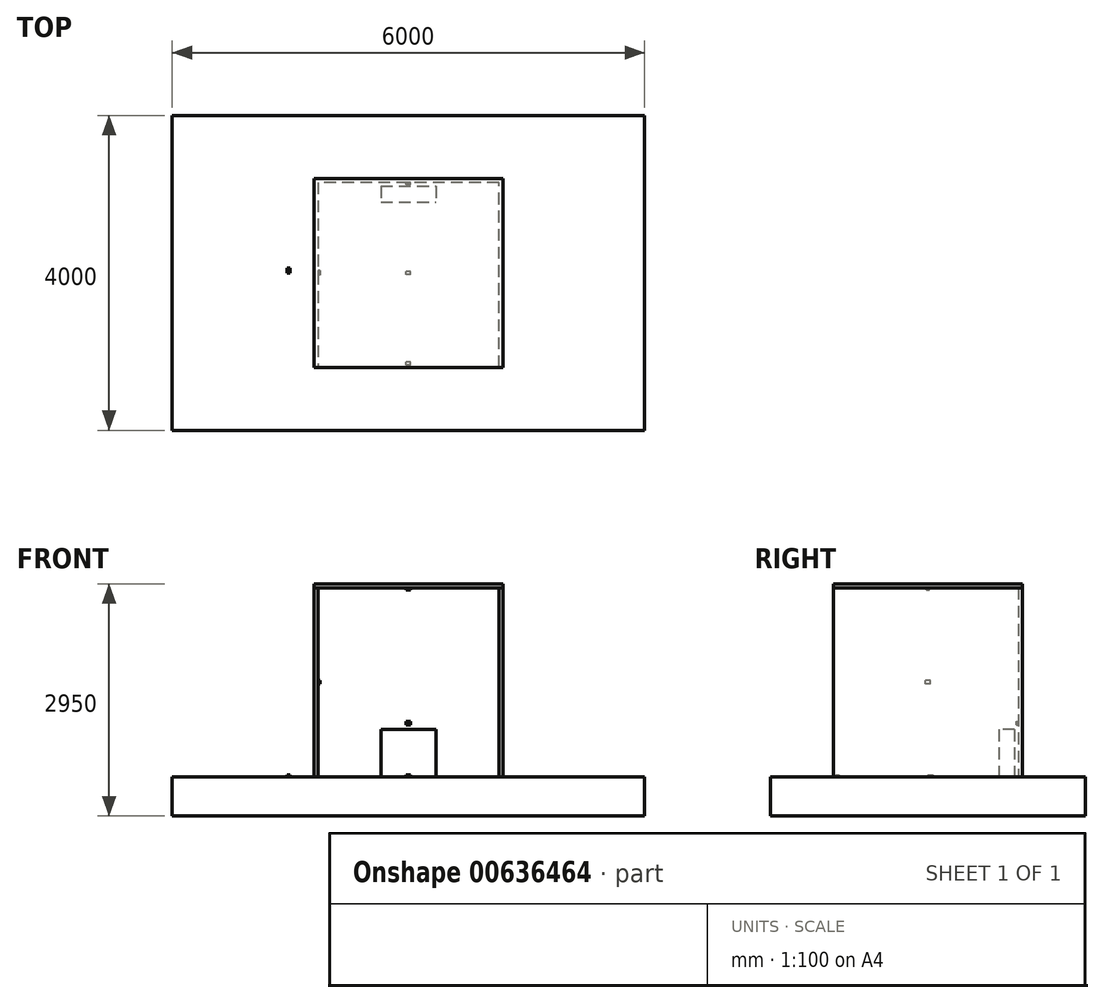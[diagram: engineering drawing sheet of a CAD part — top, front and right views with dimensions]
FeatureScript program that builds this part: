
annotation { "Feature Type Name" : "Feature", "Feature Type Description" : "" }
export const myFeature = defineFeature(function(context is Context, id is Id, definition is map)
    precondition{}
    {
        {
            var Q0;
            Q0=qCreatedBy(makeId("Top.planeOp"),FACE);
            var sketch = newSketch(context, id + "F0", { "sketchPlane" : qUnion([Q0])});
            skLineSegment(sketch, "E0.bottom", {"start": v(1200, -1200) * mm, "end": v(1150, -1200) * mm});
            skLineSegment(sketch, "E0.top", {"start": v(1200, 1200) * mm, "end": v(-1200, 1200) * mm});
            skLineSegment(sketch, "E0.left", {"start": v(1200, -1200) * mm, "end": v(1200, 1200) * mm});
            skLineSegment(sketch, "E0.right", {"start": v(-1200, -1200) * mm, "end": v(-1200, 1200) * mm});
            skPoint(sketch, "E0.middle", {"position": v(0, 0) * mm});
            skLineSegment(sketch, "E1.top", {"start": v(1150, 1150) * mm, "end": v(-1150, 1150) * mm});
            skLineSegment(sketch, "E1.left", {"start": v(1150, -1150) * mm, "end": v(1150, 1150) * mm});
            skLineSegment(sketch, "E1.right", {"start": v(-1150, -1150) * mm, "end": v(-1150, 1150) * mm});
            skLineSegment(sketch, "E2", {"start": v(-1150, -1150) * mm, "end": v(-1150, -1200) * mm});
            skLineSegment(sketch, "E3", {"start": v(1150, -1150) * mm, "end": v(1150, -1200) * mm});
            skLineSegment(sketch, "E4.trimOffspring", {"start": v(-1150, -1200) * mm, "end": v(-1200, -1200) * mm});
            skSolve(sketch);
        }
        {
            var Q0;
            Q0 = qSketchRegion(id + "F0", true);
            extrude(context, id + "F1", {"entities" : qUnion([Q0]), "endBound" : BoundingType.SYMMETRIC, "depth" : 2400 * mm, "offsetDistance" : 25 * mm});
        }
        {
            var Q0;
            Q0=makeQuery(id+"F1.opExtrude","CAP_FACE",FACE,{"disambiguationData":[OSD([sQuery(id+"F0.wireOp",EDGE,"E0.bottom"),sQuery(id+"F0.wireOp",EDGE,"E0.top"),sQuery(id+"F0.wireOp",EDGE,"E0.left"),sQuery(id+"F0.wireOp",EDGE,"E0.right"),sQuery(id+"F0.wireOp",EDGE,"E1.top"),sQuery(id+"F0.wireOp",EDGE,"E1.left"),sQuery(id+"F0.wireOp",EDGE,"E1.right"),sQuery(id+"F0.wireOp",EDGE,"E2"),sQuery(id+"F0.wireOp",EDGE,"E3"),sQuery(id+"F0.wireOp",EDGE,"E4.trimOffspring")])],"isStart":false});
            var sketch = newSketch(context, id + "F2", { "sketchPlane" : qUnion([Q0])});
            skLineSegment(sketch, "E5.bottom", {"start": v(1200, -1200) * mm, "end": v(-1200, -1200) * mm});
            skLineSegment(sketch, "E5.top", {"start": v(1200, 1200) * mm, "end": v(-1200, 1200) * mm});
            skLineSegment(sketch, "E5.left", {"start": v(1200, -1200) * mm, "end": v(1200, 1200) * mm});
            skLineSegment(sketch, "E5.right", {"start": v(-1200, -1200) * mm, "end": v(-1200, 1200) * mm});
            skSolve(sketch);
        }
        {
            var Q0;
            Q0 = qSketchRegion(id + "F2", true);
            extrude(context, id + "F3", {"entities" : qUnion([Q0]), "depth" : 50 * mm, "offsetDistance" : 25 * mm});
        }
        {
            var Q0;
            Q0=makeQuery(id+"F1.opExtrude","CAP_FACE",FACE,{"disambiguationData":[OSD([sQuery(id+"F0.wireOp",EDGE,"E0.bottom"),sQuery(id+"F0.wireOp",EDGE,"E0.top"),sQuery(id+"F0.wireOp",EDGE,"E0.left"),sQuery(id+"F0.wireOp",EDGE,"E0.right"),sQuery(id+"F0.wireOp",EDGE,"E1.top"),sQuery(id+"F0.wireOp",EDGE,"E1.left"),sQuery(id+"F0.wireOp",EDGE,"E1.right"),sQuery(id+"F0.wireOp",EDGE,"E2"),sQuery(id+"F0.wireOp",EDGE,"E3"),sQuery(id+"F0.wireOp",EDGE,"E4.trimOffspring")])],"isStart":true});
            var sketch = newSketch(context, id + "F4", { "sketchPlane" : qUnion([Q0])});
            skLineSegment(sketch, "E6.bottom", {"start": v(3000, -2000) * mm, "end": v(-3000, -2000) * mm});
            skLineSegment(sketch, "E6.top", {"start": v(3000, 2000) * mm, "end": v(-3000, 2000) * mm});
            skLineSegment(sketch, "E6.left", {"start": v(3000, -2000) * mm, "end": v(3000, 2000) * mm});
            skLineSegment(sketch, "E6.right", {"start": v(-3000, -2000) * mm, "end": v(-3000, 2000) * mm});
            skPoint(sketch, "E6.middle", {"position": v(0, 0) * mm});
            skSolve(sketch);
        }
        {
            var Q0;
            Q0 = qSketchRegion(id + "F4", true);
            extrude(context, id + "F5", {"entities" : qUnion([Q0]), "operationType" : NewBodyOperationType.ADD, "depth" : 500 * mm, "offsetDistance" : 25 * mm});
        }
        {
            var Q0;
            Q0=makeQuery(id+"F5.opExtrude","CAP_FACE",FACE,{"disambiguationData":[OSD([sQuery(id+"F4.wireOp",EDGE,"E6.bottom"),sQuery(id+"F4.wireOp",EDGE,"E6.top"),sQuery(id+"F4.wireOp",EDGE,"E6.left"),sQuery(id+"F4.wireOp",EDGE,"E6.right")])],"isStart":true});
            var sketch = newSketch(context, id + "F6", { "sketchPlane" : qUnion([Q0])});
            skLineSegment(sketch, "E7.bottom", {"start": v(-350, 1100) * mm, "end": v(350, 1100) * mm});
            skLineSegment(sketch, "E7.top", {"start": v(-350, 900) * mm, "end": v(350, 900) * mm});
            skLineSegment(sketch, "E7.left", {"start": v(-350, 1100) * mm, "end": v(-350, 900) * mm});
            skLineSegment(sketch, "E7.right", {"start": v(350, 1100) * mm, "end": v(350, 900) * mm});
            skSolve(sketch);
        }
        {
            var Q0;
            Q0 = qSketchRegion(id + "F6", true);
            extrude(context, id + "F7", {"entities" : qUnion([Q0]), "depth" : 600 * mm, "offsetDistance" : 25 * mm});
        }
        {
            var Q0;
            Q0=makeQuery(id+"F5.opExtrude","CAP_FACE",FACE,{"disambiguationData":[OSD([sQuery(id+"F4.wireOp",EDGE,"E6.bottom"),sQuery(id+"F4.wireOp",EDGE,"E6.top"),sQuery(id+"F4.wireOp",EDGE,"E6.left"),sQuery(id+"F4.wireOp",EDGE,"E6.right")])],"isStart":true});
            var sketch = newSketch(context, id + "F8", { "sketchPlane" : qUnion([Q0])});
            skLineSegment(sketch, "E8.bottom", {"start": v(30, -1170) * mm, "end": v(-30, -1170) * mm});
            skLineSegment(sketch, "E8.top", {"start": v(30, -1130) * mm, "end": v(-30, -1130) * mm});
            skLineSegment(sketch, "E8.left", {"start": v(30, -1170) * mm, "end": v(30, -1130) * mm});
            skLineSegment(sketch, "E8.right", {"start": v(-30, -1170) * mm, "end": v(-30, -1130) * mm});
            skPoint(sketch, "E8.middle", {"position": v(0, -1150) * mm});
            skSolve(sketch);
        }
        {
            var Q0;
            Q0 = qSketchRegion(id + "F8", true);
            extrude(context, id + "F9", {"entities" : qUnion([Q0]), "depth" : 25 * mm, "offsetDistance" : 25 * mm});
        }
        {
            var Q0;
            Q0=makeQuery(id+"F1.opExtrude","SWEPT_FACE",FACE,{"disambiguationData":[OSD([sQuery(id+"F0.wireOp",EDGE,"E1.top")])]});
            var sketch = newSketch(context, id + "F10", { "sketchPlane" : qUnion([Q0])});
            skLineSegment(sketch, "E9.bottom", {"start": v(30, -540) * mm, "end": v(-30, -540) * mm});
            skLineSegment(sketch, "E9.top", {"start": v(30, -500) * mm, "end": v(-30, -500) * mm});
            skLineSegment(sketch, "E9.left", {"start": v(30, -540) * mm, "end": v(30, -500) * mm});
            skLineSegment(sketch, "E9.right", {"start": v(-30, -540) * mm, "end": v(-30, -500) * mm});
            skPoint(sketch, "E9.middle", {"position": v(0, -520) * mm});
            skSolve(sketch);
        }
        {
            var Q0;
            Q0 = qSketchRegion(id + "F10", true);
            extrude(context, id + "F11", {"entities" : qUnion([Q0]), "depth" : 25 * mm, "offsetDistance" : 25 * mm});
        }
        {
            var Q0;
            Q0=makeQuery(id+"F1.opExtrude","SWEPT_FACE",FACE,{"disambiguationData":[OSD([sQuery(id+"F0.wireOp",EDGE,"E1.right"),sQuery(id+"F0.wireOp",EDGE,"E2")])]});
            var sketch = newSketch(context, id + "F12", { "sketchPlane" : qUnion([Q0])});
            skLineSegment(sketch, "E10.bottom", {"start": v(30, -20) * mm, "end": v(-30, -20) * mm});
            skLineSegment(sketch, "E10.top", {"start": v(30, 20) * mm, "end": v(-30, 20) * mm});
            skLineSegment(sketch, "E10.left", {"start": v(30, -20) * mm, "end": v(30, 20) * mm});
            skLineSegment(sketch, "E10.right", {"start": v(-30, -20) * mm, "end": v(-30, 20) * mm});
            skPoint(sketch, "E10.middle", {"position": v(0, 0) * mm});
            skSolve(sketch);
        }
        {
            var Q0;
            Q0 = qSketchRegion(id + "F12", true);
            extrude(context, id + "F13", {"entities" : qUnion([Q0]), "depth" : 25 * mm, "offsetDistance" : 25 * mm});
        }
        {
            var Q0;
            Q0=makeQuery(id+"F3.opExtrude","CAP_FACE",FACE,{"disambiguationData":[OSD([sQuery(id+"F2.wireOp",EDGE,"E5.bottom"),sQuery(id+"F2.wireOp",EDGE,"E5.top"),sQuery(id+"F2.wireOp",EDGE,"E5.left"),sQuery(id+"F2.wireOp",EDGE,"E5.right")])],"isStart":true});
            var sketch = newSketch(context, id + "F14", { "sketchPlane" : qUnion([Q0])});
            skLineSegment(sketch, "E11.bottom", {"start": v(30, 20) * mm, "end": v(-30, 20) * mm});
            skLineSegment(sketch, "E11.top", {"start": v(30, -20) * mm, "end": v(-30, -20) * mm});
            skLineSegment(sketch, "E11.left", {"start": v(30, 20) * mm, "end": v(30, -20) * mm});
            skLineSegment(sketch, "E11.right", {"start": v(-30, 20) * mm, "end": v(-30, -20) * mm});
            skPoint(sketch, "E11.middle", {"position": v(0, 0) * mm});
            skSolve(sketch);
        }
        {
            var Q0;
            Q0 = qSketchRegion(id + "F14", true);
            extrude(context, id + "F15", {"entities" : qUnion([Q0]), "depth" : 25 * mm, "offsetDistance" : 25 * mm});
        }
        {
            var Q0;
            Q0=makeQuery(id+"F5.opExtrude","CAP_FACE",FACE,{"disambiguationData":[OSD([sQuery(id+"F4.wireOp",EDGE,"E6.bottom"),sQuery(id+"F4.wireOp",EDGE,"E6.top"),sQuery(id+"F4.wireOp",EDGE,"E6.left"),sQuery(id+"F4.wireOp",EDGE,"E6.right")])],"isStart":true});
            var sketch = newSketch(context, id + "F16", { "sketchPlane" : qUnion([Q0])});
            skLineSegment(sketch, "E12.bottom", {"start": v(-1540, 0) * mm, "end": v(-1500, 0) * mm});
            skLineSegment(sketch, "E12.top", {"start": v(-1540, 60) * mm, "end": v(-1500, 60) * mm});
            skLineSegment(sketch, "E12.left", {"start": v(-1540, 0) * mm, "end": v(-1540, 60) * mm});
            skLineSegment(sketch, "E12.right", {"start": v(-1500, 0) * mm, "end": v(-1500, 60) * mm});
            skPoint(sketch, "E12.middle", {"position": v(-1520, 30) * mm});
            skSolve(sketch);
        }
        {
            var Q0;
            Q0 = qSketchRegion(id + "F16", true);
            extrude(context, id + "F17", {"entities" : qUnion([Q0]), "depth" : 25 * mm, "offsetDistance" : 25 * mm});
        }
    });
